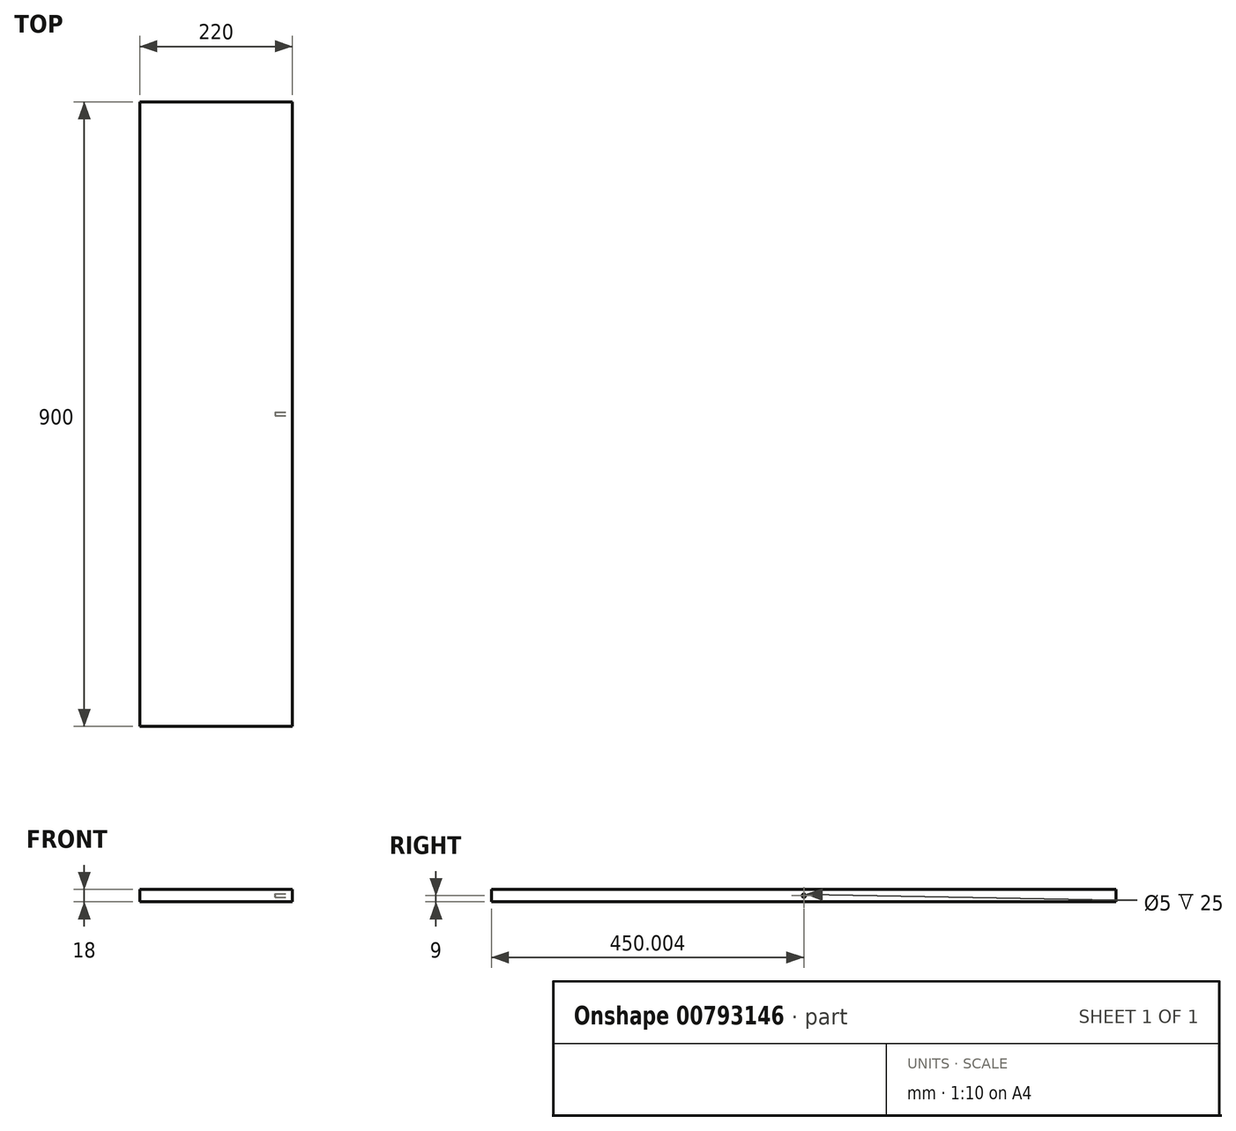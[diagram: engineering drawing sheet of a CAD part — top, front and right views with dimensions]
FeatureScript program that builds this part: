
annotation { "Feature Type Name" : "Feature", "Feature Type Description" : "" }
export const myFeature = defineFeature(function(context is Context, id is Id, definition is map)
    precondition{}
    {
        {
            var Q0;
            Q0=qCreatedBy(makeId("Top.planeOp"),FACE);
            var sketch = newSketch(context, id + "F0", { "sketchPlane" : qUnion([Q0])});
            skLineSegment(sketch, "E0.bottom", {"start": v(-133.49, 863.14) * mm, "end": v(86.51, 863.14) * mm});
            skLineSegment(sketch, "E0.top", {"start": v(-133.49, -36.86) * mm, "end": v(86.51, -36.86) * mm});
            skLineSegment(sketch, "E0.left", {"start": v(-133.49, 863.14) * mm, "end": v(-133.49, -36.86) * mm});
            skLineSegment(sketch, "E0.right", {"start": v(86.51, 863.14) * mm, "end": v(86.51, -36.86) * mm});
            skSolve(sketch);
        }
        {
            var Q0;
            Q0=makeQuery(id+"F0.imprint","IMPRINT",FACE,{"disambiguationData":[TD([[makeQuery(id+"F0.imprint","IMPRINT",EDGE,{"derivedFrom":sQuery(id+"F0.wireOp",EDGE,"E0.bottom")}),-1.0]])]});
            extrude(context, id + "F1", {"entities" : qUnion([Q0]), "depth" : 18 * mm, "offsetDistance" : 25 * mm});
        }
        {
            var Q0;
            Q0=makeQuery(id+"F1.opExtrude","SWEPT_FACE",FACE,{"disambiguationData":[OSD([sQuery(id+"F0.wireOp",EDGE,"E0.right")])]});
            var sketch = newSketch(context, id + "F2", { "sketchPlane" : qUnion([Q0])});
            skCircle(sketch, "E1", {"center": v(413.14, 9) * mm, "radius": 2.5 * mm});
            skPoint(sketch, "E1.centerSnap0", {"position": v(413.14, 0) * mm});
            skSolve(sketch);
        }
        {
            var Q0;
            Q0 = qSketchRegion(id + "F2", true);
            extrude(context, id + "F3", {"entities" : qUnion([Q0]), "operationType" : NewBodyOperationType.REMOVE, "oppositeDirection" : true, "depth" : 25 * mm, "offsetDistance" : 25 * mm});
        }
    });
